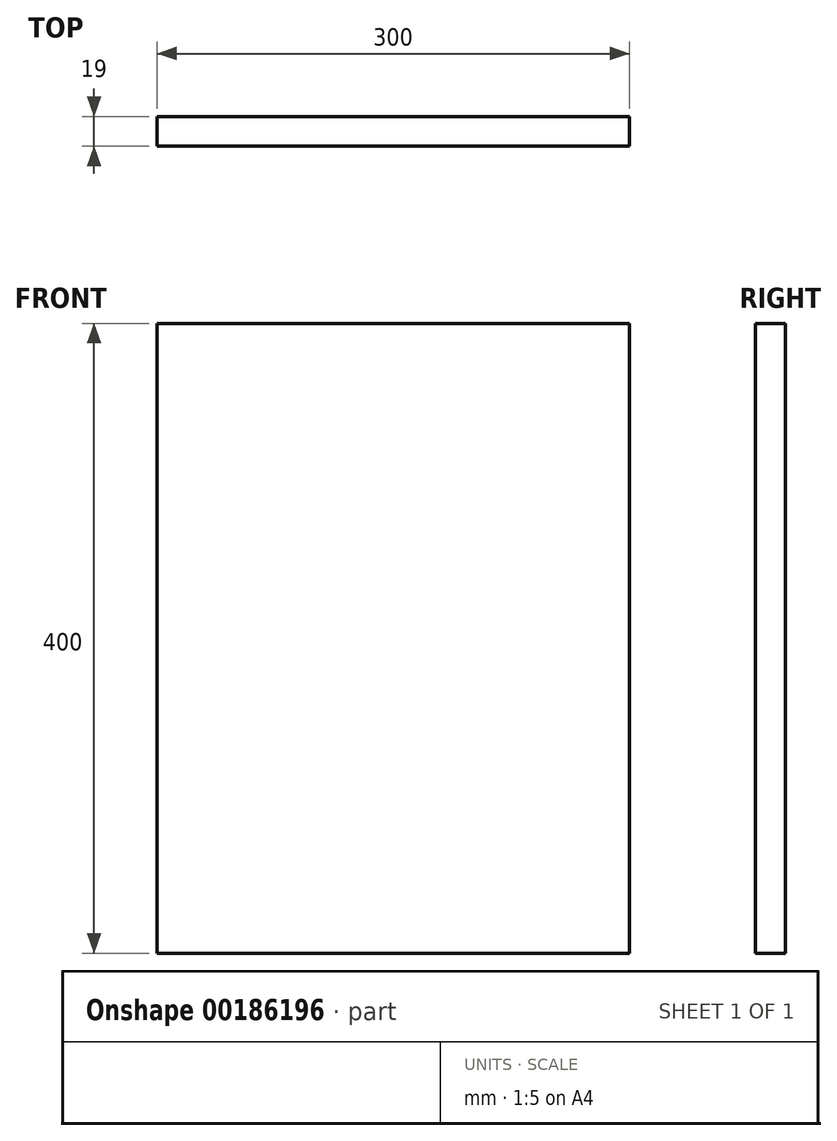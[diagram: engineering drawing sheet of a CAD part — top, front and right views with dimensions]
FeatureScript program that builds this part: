
annotation { "Feature Type Name" : "Feature", "Feature Type Description" : "" }
export const myFeature = defineFeature(function(context is Context, id is Id, definition is map)
    precondition{}
    {
        {
            var Q0;
            Q0=qCreatedBy(makeId("Front.planeOp"),FACE);
            var sketch = newSketch(context, id + "F0", { "sketchPlane" : qUnion([Q0])});
            skLineSegment(sketch, "E0.bottom", {"start": v(-159.67, 210.5) * mm, "end": v(140.33, 210.5) * mm});
            skLineSegment(sketch, "E0.top", {"start": v(-159.67, -189.5) * mm, "end": v(140.33, -189.5) * mm});
            skLineSegment(sketch, "E0.left", {"start": v(-159.67, 210.5) * mm, "end": v(-159.67, -189.5) * mm});
            skLineSegment(sketch, "E0.right", {"start": v(140.33, 210.5) * mm, "end": v(140.33, -189.5) * mm});
            skSolve(sketch);
        }
        {
            var Q0;
            Q0 = qSketchRegion(id + "F0", true);
            extrude(context, id + "F1", {"entities" : qUnion([Q0]), "depth" : 19 * mm});
        }
    });
